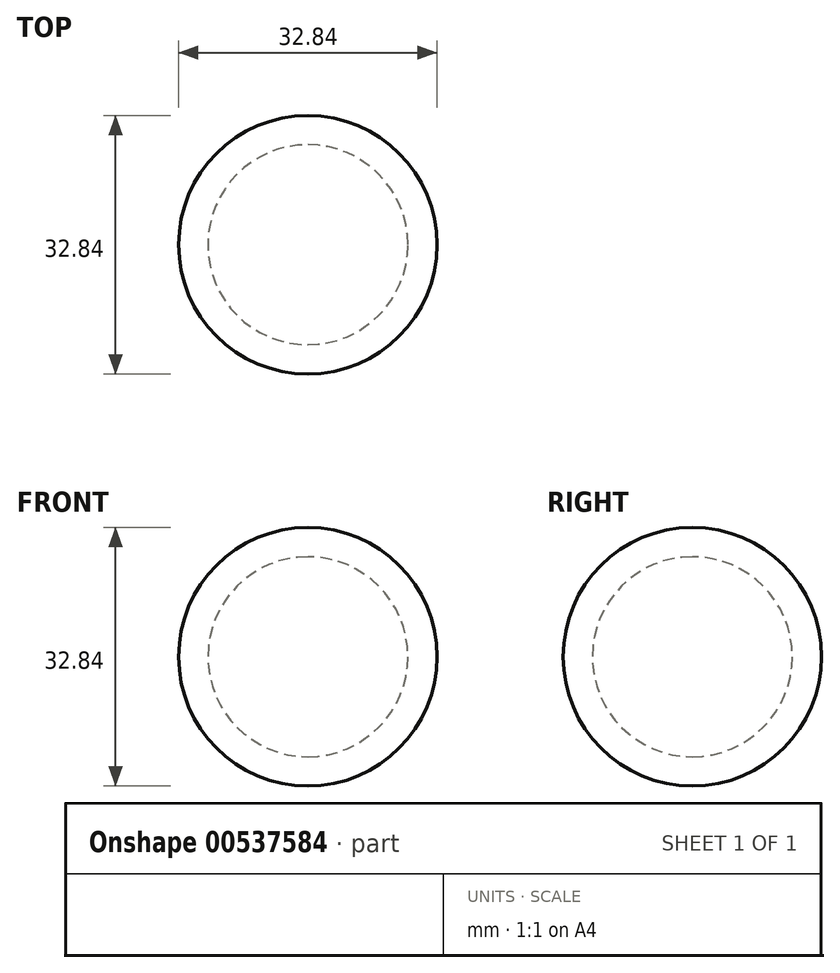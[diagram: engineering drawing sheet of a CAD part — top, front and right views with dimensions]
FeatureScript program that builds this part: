
annotation { "Feature Type Name" : "Feature", "Feature Type Description" : "" }
export const myFeature = defineFeature(function(context is Context, id is Id, definition is map)
    precondition{}
    {
        {
            var Q0;
            Q0=qCreatedBy(makeId("Front.planeOp"),FACE);
            var sketch = newSketch(context, id + "F0", { "sketchPlane" : qUnion([Q0])});
            skArc(sketch, "E0", {"start": v(0, 12.7) * mm, "mid": v(-12.7, 0) * mm, "end": v(0, -12.7) * mm});
            skArc(sketch, "E1", {"start": v(0, 16.42) * mm, "mid": v(-16.42, 0) * mm, "end": v(0, -16.42) * mm});
            skLineSegment(sketch, "E2", {"start": v(0, 16.42) * mm, "end": v(0, 12.7) * mm});
            skLineSegment(sketch, "E3.trimOffspring", {"start": v(0, -12.7) * mm, "end": v(0, -16.42) * mm});
            skSolve(sketch);
        }
        {
            var Q0;
            Q0 = qSketchRegion(id + "F0", true);
            var Q1;
            Q1=sQuery(id+"F0.wireOp",EDGE,"E3.trimOffspring");
            revolve(context, id + "F1", {"entities" : qUnion([Q0]), "axis" : qUnion([Q1]), "revolveType" : RevolveType.FULL});
        }
    });
